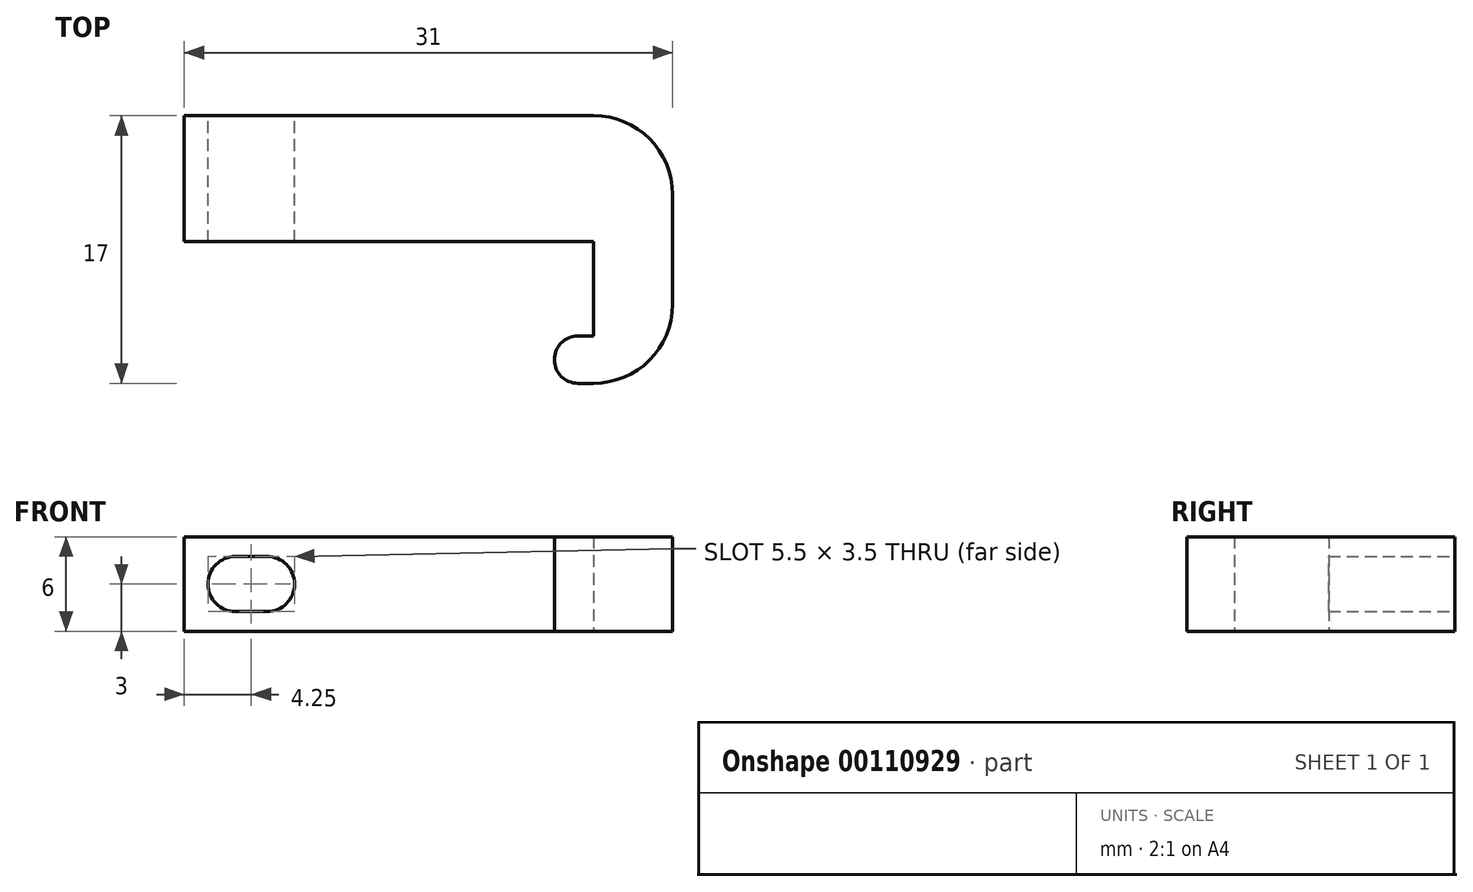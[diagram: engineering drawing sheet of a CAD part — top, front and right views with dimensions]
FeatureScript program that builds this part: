
annotation { "Feature Type Name" : "Feature", "Feature Type Description" : "" }
export const myFeature = defineFeature(function(context is Context, id is Id, definition is map)
    precondition{}
    {
        {
            var Q0;
            Q0=qCreatedBy(makeId("Top.planeOp"),FACE);
            var sketch = newSketch(context, id + "F0", { "sketchPlane" : qUnion([Q0])});
            skLineSegment(sketch, "E0", {"start": v(0, 0) * mm, "end": v(5, 0) * mm});
            skLineSegment(sketch, "E1", {"start": v(5, 0) * mm, "end": v(5, 17) * mm});
            skLineSegment(sketch, "E2", {"start": v(5, 17) * mm, "end": v(-26, 17) * mm});
            skLineSegment(sketch, "E3", {"start": v(-26, 17) * mm, "end": v(-26, 9) * mm});
            skLineSegment(sketch, "E4", {"start": v(-26, 9) * mm, "end": v(0, 9) * mm});
            skLineSegment(sketch, "E5", {"start": v(0, 9) * mm, "end": v(0, 3) * mm});
            skLineSegment(sketch, "E6", {"start": v(0, 3) * mm, "end": v(-1, 3) * mm});
            skLineSegment(sketch, "E7", {"start": v(0, 0) * mm, "end": v(-1, 0) * mm});
            skArc(sketch, "E8", {"start": v(-1, 3) * mm, "mid": v(-2.5, 1.5) * mm, "end": v(-1, 0) * mm});
            skSolve(sketch);
        }
        {
            var Q0;
            Q0=qSketchRegion(id+"F0",true);
            extrude(context, id + "F1", {"entities" : qUnion([Q0]), "depth" : 6 * mm});
        }
        {
            var Q0;
            Q0=makeQuery(id+"F1.opExtrude","SWEPT_FACE",FACE,{"disambiguationData":[OSD([sQuery(id+"F0.wireOp",EDGE,"E2")])]});
            var sketch = newSketch(context, id + "F2", { "sketchPlane" : qUnion([Q0])});
            skCircle(sketch, "E9", {"center": v(22.75, 3) * mm, "radius": 1.75 * mm});
            skLineSegment(sketch, "E10", {"start": v(22.75, 6) * mm, "end": v(22.75, 0) * mm});
            skCircle(sketch, "E11", {"center": v(20.75, 3) * mm, "radius": 1.75 * mm});
            skLineSegment(sketch, "E12", {"start": v(20.75, 4.75) * mm, "end": v(22.75, 4.75) * mm});
            skLineSegment(sketch, "E13", {"start": v(20.75, 1.25) * mm, "end": v(22.75, 1.25) * mm});
            skSolve(sketch);
        }
        {
            var Q0;
            Q0=qSketchRegion(id+"F2",true);
            var Q1;
            {var subQ0=sQuery(id+"F2.wireOp",EDGE,"E11");var subQ1=sQuery(id+"F2.wireOp",EDGE,"E9");var subQ3=makeQuery(id+"F2.imprint","INTERSECT",VERTEX,{"disambiguationData":[OD(0.0)],"derivedFrom":[subQ1,subQ0]});Q1=makeQuery(id+"F2.imprint","IMPRINT",FACE,{"disambiguationData":[TD([[makeQuery(id+"F2.imprint","IMPRINT",EDGE,{"disambiguationData":[TD([[subQ3,-1.0]])],"derivedFrom":subQ1}),1.0]])]});}
            var Q2;
            {var subQ1=sQuery(id+"F2.wireOp",EDGE,"E9");var subQ3=sQuery(id+"F2.wireOp",EDGE,"E11");var subQ4=makeQuery(id+"F2.imprint","INTERSECT",VERTEX,{"disambiguationData":[OD(0.0)],"derivedFrom":[subQ1,subQ3]});Q2=makeQuery(id+"F2.imprint","IMPRINT",FACE,{"disambiguationData":[TD([[makeQuery(id+"F2.imprint","IMPRINT",EDGE,{"disambiguationData":[TD([[subQ4,1.0]])],"derivedFrom":subQ3}),-1.0]])]});}
            extrude(context, id + "F3", {"entities" : qUnion([Q0, Q1, Q2]), "operationType" : NewBodyOperationType.REMOVE, "oppositeDirection" : true, "depth" : 25 * mm});
        }
        {
            var Q0;
            Q0=makeQuery(id+"F1.opExtrude","SWEPT_EDGE",EDGE,{"disambiguationData":[OSD([sQuery(id+"F0.wireOp",EDGE,"E1"),sQuery(id+"F0.wireOp",EDGE,"E2")])]});
            var Q1;
            Q1=makeQuery(id+"F1.opExtrude","SWEPT_EDGE",EDGE,{"disambiguationData":[OSD([sQuery(id+"F0.wireOp",EDGE,"E0"),sQuery(id+"F0.wireOp",EDGE,"E1")])]});
            fillet(context, id + "F4", {"entities" : qUnion([Q0, Q1]), "radius" : 5 * mm, "tangentPropagation" : true, "allowEdgeOverflow" : false});
        }
    });
